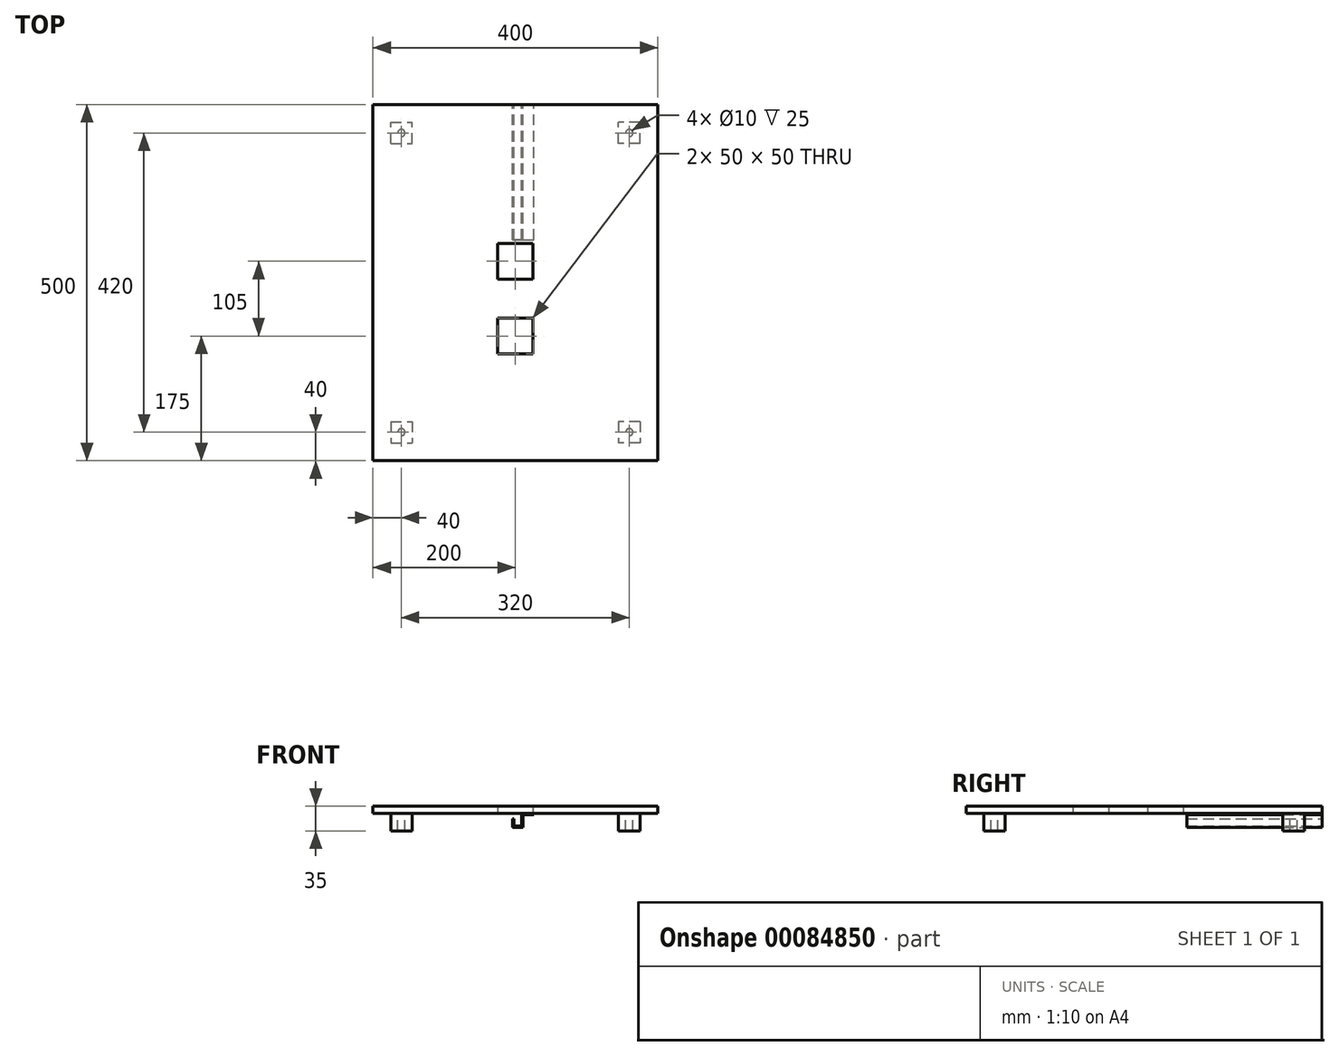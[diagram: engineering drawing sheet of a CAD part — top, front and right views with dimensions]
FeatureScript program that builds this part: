
annotation { "Feature Type Name" : "Feature", "Feature Type Description" : "" }
export const myFeature = defineFeature(function(context is Context, id is Id, definition is map)
    precondition{}
    {
        {
            var Q0;
            Q0=qCreatedBy(makeId("Top.planeOp"),FACE);
            var sketch = newSketch(context, id + "F0", { "sketchPlane" : qUnion([Q0])});
            skLineSegment(sketch, "E0.bottom", {"start": v(-200, 250) * mm, "end": v(200, 250) * mm});
            skLineSegment(sketch, "E0.top", {"start": v(-200, -250) * mm, "end": v(200, -250) * mm});
            skLineSegment(sketch, "E0.left", {"start": v(-200, 250) * mm, "end": v(-200, -250) * mm});
            skLineSegment(sketch, "E0.right", {"start": v(200, 250) * mm, "end": v(200, -250) * mm});
            skLineSegment(sketch, "E1", {"start": v(0, -250) * mm, "end": v(0, 0) * mm, "construction": true});
            skLineSegment(sketch, "E2", {"start": v(0, 0) * mm, "end": v(0, 0) * mm});
            skPoint(sketch, "E3.rect.middle", {"position": v(0, 0) * mm});
            skLineSegment(sketch, "E4", {"start": v(0, 0) * mm, "end": v(-200, 0) * mm, "construction": true});
            skPoint(sketch, "E5", {"position": v(0, -75) * mm});
            skLineSegment(sketch, "E6.rect.bottom", {"start": v(25, -100) * mm, "end": v(-25, -100) * mm});
            skLineSegment(sketch, "E6.rect.top", {"start": v(25, -50) * mm, "end": v(-25, -50) * mm});
            skLineSegment(sketch, "E6.rect.left", {"start": v(25, -100) * mm, "end": v(25, -50) * mm});
            skLineSegment(sketch, "E6.rect.right", {"start": v(-25, -100) * mm, "end": v(-25, -50) * mm});
            skLineSegment(sketch, "E7.rect.bottom", {"start": v(25, 5) * mm, "end": v(-25, 5) * mm});
            skLineSegment(sketch, "E7.rect.top", {"start": v(25, 55) * mm, "end": v(-25, 55) * mm});
            skLineSegment(sketch, "E7.rect.left", {"start": v(25, 5) * mm, "end": v(25, 55) * mm});
            skLineSegment(sketch, "E7.rect.right", {"start": v(-25, 5) * mm, "end": v(-25, 55) * mm});
            skPoint(sketch, "E8.rect.middle", {"position": v(0, 30) * mm});
            skSolve(sketch);
        }
        {
            var Q0;
            Q0=qSketchRegion(id+"F0",true);
            extrude(context, id + "F1", {"entities" : qUnion([Q0]), "depth" : 10 * mm});
        }
        {
            var Q0;
            Q0=makeQuery(id+"F1.opExtrude","CAP_FACE",FACE,{"disambiguationData":[OSD([sQuery(id+"F0.wireOp",EDGE,"E0.bottom"),sQuery(id+"F0.wireOp",EDGE,"E0.top"),sQuery(id+"F0.wireOp",EDGE,"E0.left"),sQuery(id+"F0.wireOp",EDGE,"E0.right"),sQuery(id+"F0.wireOp",EDGE,"6f9bbaf3-54c9-45fb-8255-ebd578459f4e"),sQuery(id+"F0.wireOp",EDGE,"572baf31-667b-4c5a-b74f-dafc37ab3cf4")])],"isStart":true});
            var sketch = newSketch(context, id + "F2", { "sketchPlane" : qUnion([Q0])});
            skLineSegment(sketch, "E9.rect.bottom", {"start": v(175, 195) * mm, "end": v(145, 195) * mm});
            skLineSegment(sketch, "E9.rect.top", {"start": v(175, 225) * mm, "end": v(145, 225) * mm});
            skLineSegment(sketch, "E9.rect.left", {"start": v(175, 195) * mm, "end": v(175, 225) * mm});
            skLineSegment(sketch, "E9.rect.right", {"start": v(145, 195) * mm, "end": v(145, 225) * mm});
            skPoint(sketch, "E9.rect.middle", {"position": v(160, 210) * mm});
            skCircle(sketch, "E10", {"center": v(160, 210) * mm, "radius": 5 * mm});
            skLineSegment(sketch, "E11", {"start": v(0, 0) * mm, "end": v(200, 0) * mm, "construction": true});
            skLineSegment(sketch, "E12", {"start": v(0, 0) * mm, "end": v(0, 250) * mm, "construction": true});
            skCircle(sketch, "E13.MirrorC", {"center": v(160, -210) * mm, "radius": 5 * mm});
            skLineSegment(sketch, "E14.MirrorCS", {"start": v(145, -195) * mm, "end": v(145, -225) * mm});
            skLineSegment(sketch, "E15.MirrorCS", {"start": v(175, -195) * mm, "end": v(145, -195) * mm});
            skLineSegment(sketch, "E16.MirrorCS", {"start": v(175, -195) * mm, "end": v(175, -225) * mm});
            skLineSegment(sketch, "E17.MirrorCS", {"start": v(175, -225) * mm, "end": v(145, -225) * mm});
            skCircle(sketch, "E18.MirrorC", {"center": v(-160, 210) * mm, "radius": 5 * mm});
            skCircle(sketch, "E19.MirrorC", {"center": v(-160, -210) * mm, "radius": 5 * mm});
            skLineSegment(sketch, "E20.MirrorCS", {"start": v(-145, -195) * mm, "end": v(-145, -225) * mm});
            skLineSegment(sketch, "E21.MirrorCS", {"start": v(-145, 195) * mm, "end": v(-145, 225) * mm});
            skLineSegment(sketch, "E22.MirrorCS", {"start": v(-175, 195) * mm, "end": v(-145, 195) * mm});
            skLineSegment(sketch, "E23.MirrorCS", {"start": v(-175, 225) * mm, "end": v(-145, 225) * mm});
            skLineSegment(sketch, "E24.MirrorCS", {"start": v(-175, 195) * mm, "end": v(-175, 225) * mm});
            skLineSegment(sketch, "E25.MirrorCS", {"start": v(-175, -195) * mm, "end": v(-145, -195) * mm});
            skLineSegment(sketch, "E26.MirrorCS", {"start": v(-175, -195) * mm, "end": v(-175, -225) * mm});
            skLineSegment(sketch, "E27.MirrorCS", {"start": v(-175, -225) * mm, "end": v(-145, -225) * mm});
            skSolve(sketch);
        }
        {
            var Q0;
            Q0=qSketchRegion(id+"F2",true);
            extrude(context, id + "F3", {"entities" : qUnion([Q0]), "operationType" : NewBodyOperationType.ADD, "depth" : 25 * mm});
        }
        {
            var Q0;
            Q0=makeQuery(id+"F1.opExtrude","SWEPT_FACE",FACE,{"disambiguationData":[OSD([sQuery(id+"F0.wireOp",EDGE,"E0.bottom")])]});
            var sketch = newSketch(context, id + "F4", { "sketchPlane" : qUnion([Q0])});
            skLineSegment(sketch, "E28", {"start": v(4, -8) * mm, "end": v(4, -20) * mm});
            skLineSegment(sketch, "E29", {"start": v(4, -20) * mm, "end": v(-11, -20) * mm});
            skLineSegment(sketch, "E30", {"start": v(2, -18) * mm, "end": v(2, -8) * mm});
            skLineSegment(sketch, "E31", {"start": v(2, -8) * mm, "end": v(4, -8) * mm});
            skLineSegment(sketch, "E32.left", {"start": v(-9, 0) * mm, "end": v(-9, -18) * mm});
            skLineSegment(sketch, "E33", {"start": v(-9, -18) * mm, "end": v(2, -18) * mm});
            skLineSegment(sketch, "E34", {"start": v(-11, -20) * mm, "end": v(-11, -2) * mm});
            skLineSegment(sketch, "E35", {"start": v(-11, -2) * mm, "end": v(-26, -2) * mm});
            skLineSegment(sketch, "E36", {"start": v(-26, -2) * mm, "end": v(-26, 0) * mm});
            skLineSegment(sketch, "E37", {"start": v(-26, 0) * mm, "end": v(-9, 0) * mm});
            skSolve(sketch);
        }
        {
            var Q0;
            Q0=qSketchRegion(id+"F4",true);
            var Q1;
            {var subQ0=sQuery(id+"F0.wireOp",EDGE,"E0.left");var subQ1=sQuery(id+"F0.wireOp",EDGE,"E6.rect.top");var subQ2=sQuery(id+"F0.wireOp",EDGE,"E0.top");var subQ3=sQuery(id+"F0.wireOp",EDGE,"E7.rect.right");var subQ4=sQuery(id+"F0.wireOp",EDGE,"E7.rect.left");var subQ5=sQuery(id+"F0.wireOp",EDGE,"E0.right");var subQ6=sQuery(id+"F0.wireOp",EDGE,"E0.bottom");var subQ7=sQuery(id+"F0.wireOp",EDGE,"E7.rect.bottom");var subQ8=sQuery(id+"F0.wireOp",EDGE,"E6.rect.bottom");var subQ9=sQuery(id+"F0.wireOp",EDGE,"E6.rect.left");var subQ10=sQuery(id+"F0.wireOp",EDGE,"E6.rect.right");var subQ11=sQuery(id+"F0.wireOp",EDGE,"E7.rect.top");Q1=makeQuery(id+"F3.boolean.opBoolean","SPLIT",FACE,{"disambiguationData":[TD([makeQuery(id+"F1.opExtrude","SWEPT_FACE",FACE,{"disambiguationData":[OSD([subQ6])]})])],"derivedFrom":makeQuery(id+"F1.opExtrude","CAP_FACE",FACE,{"disambiguationData":[OSD([subQ6,subQ2,subQ0,subQ5,subQ8,subQ1,subQ9,subQ10,subQ7,subQ11,subQ4,subQ3])],"isStart":true})});}
            extrude(context, id + "F5", {"entities" : qUnion([Q0]), "operationType" : NewBodyOperationType.ADD, "oppositeDirection" : true, "endBoundEntityFace" : qUnion([Q1]), "depth" : 190 * mm});
        }
    });
